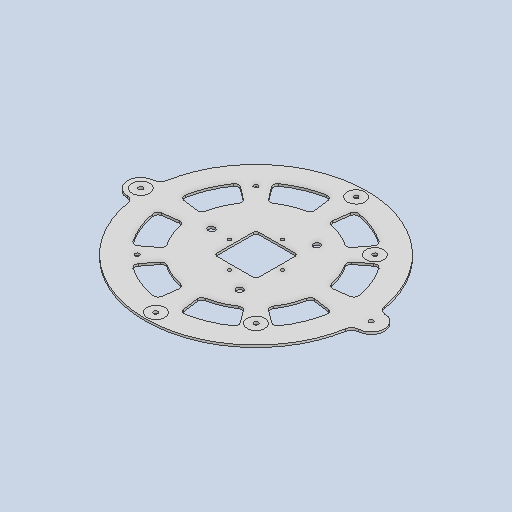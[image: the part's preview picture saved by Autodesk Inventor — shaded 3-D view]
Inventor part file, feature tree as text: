
AUTODESK INVENTOR PART (.ipt)
format: ipt  version: 2025.1 (Build 291241020, 241B)  size: 944,640 bytes
history: native  units: in
note: dims shown in document units (in); Inventor stores cm internally (conversion verified against a paired STEP export)
features: sketch x8, extrude x5, split x3, fillet x2
ambient origin geometry x8: Origin, YZ Plane, XZ Plane, XY Plane, X Axis, Y Axis, Z Axis, Center Point
bodies: Solid35 (feature_tree), Solid40 (feature_tree), Solid41 (feature_tree)
feature tree (18):
  extrude  "Extrusion1"  Depth=2.3661in
  fillet  "Fillet1"  Radius=2.3661in
  extrude  "Extrusion3"  Depth=2.3661in
  extrude  "Extrusion2"  Depth=0.1575in
  fillet  "Fillet5"  Radius=0.201in
  sketch  "Sketch5"  dims[d10=0.201in d11=2.9921in]
  split  "Split17"
  split  "Split18"
  split  "Split19"
  sketch  "Sketch8"  dims[d13=2.9921in]
  sketch  "Sketch9"  dims[d14=1.4961in d15=0.375in d17=4.358in d20=0.375in d24=0.2525in d25=0.2525in d26=11.311in d27=5.6555in d30=1.5in d31=0.2525in d33=13.01in d34=0.125in d35=0.0in d36=0.4in d38=4.358in d39=4.358in d41=5.0322in d54=0.25in d55=0.0in d79=0.25in d80=0.25in d81=0.25in d82=0.25in d83=9.5in d84=6.7175in d85=6.7175in d86=9.5in d87=0.25in d88=0.0in d94=3.3588in d95=3.3588in d96=10.0in d97=7.25in d98=15.0deg d99=0.2577in d100=3.1496in d102=360.0deg d104=0.25in d107=0.125in d108=0.125in d109=0.125in d119=0.4573in d120=0.4162in d121=0.3519in d122=0.6651in d123=0.379in d124=0.2188in d125=0.383in d126=0.735in d127=0.5332in d128=0.2522in d129=0.3287in d130=0.0218in d131=0.125in d132=0.3485in d133=0.0777in d135=1.0in d136=1.0in d137=1.0in d138=1.0in d139=1.0in d140=1.0in d141=1.0in d142=1.0in d143=0.0in d144=0.0in d145=0.0in d146=0.0in d147=1.0in d148=1.0in d149=1.0in d150=1.0in]
  extrude  "Extrusion4"  Depth=0.201in
  extrude  "Extrusion5"  Depth=2.9921in
  sketch  "Sketch1"  dims[d0=12.5in d1=1.1831in d2=2.3661in]
  sketch  "Sketch2"  dims[d3=2.3661in d4=1.1831in]
  sketch  "Sketch4"  dims[d5=0.1575in d6=0.1575in d7=0.201in]
  sketch  "Sketch Circular Pattern4"  dims[d8=0.201in d9=0.201in]
  sketch  "Sketch6"  dims[d12=1.4961in]
